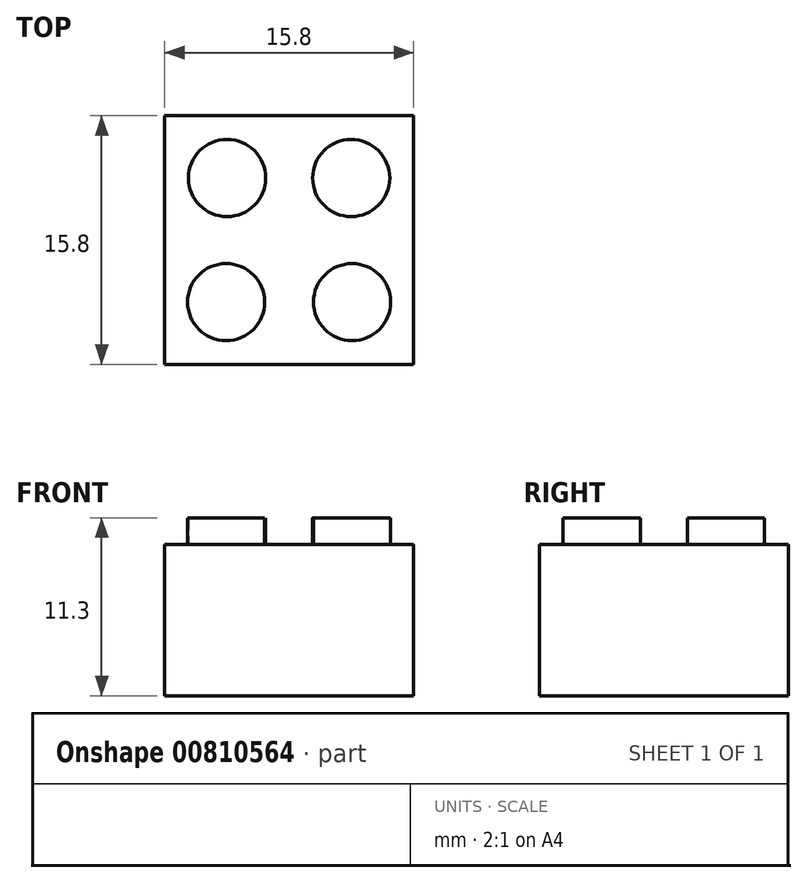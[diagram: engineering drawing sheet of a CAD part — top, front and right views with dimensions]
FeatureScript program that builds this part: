
annotation { "Feature Type Name" : "Feature", "Feature Type Description" : "" }
export const myFeature = defineFeature(function(context is Context, id is Id, definition is map)
    precondition{}
    {
        {
            var Q0;
            Q0=qCreatedBy(makeId("Top.planeOp"),FACE);
            var sketch = newSketch(context, id + "F0", { "sketchPlane" : qUnion([Q0])});
            skLineSegment(sketch, "E0", {"start": v(0, 0) * mm, "end": v(0, 15.8) * mm});
            skLineSegment(sketch, "E1", {"start": v(0, 15.8) * mm, "end": v(15.8, 15.8) * mm});
            skLineSegment(sketch, "E2", {"start": v(15.8, 15.8) * mm, "end": v(15.8, 0) * mm});
            skLineSegment(sketch, "E3", {"start": v(15.8, 0) * mm, "end": v(0, 0) * mm});
            skSolve(sketch);
        }
        {
            var Q0;
            Q0=makeQuery(id+"F0.imprint","IMPRINT",FACE,{"disambiguationData":[TD([[makeQuery(id+"F0.imprint","IMPRINT",EDGE,{"derivedFrom":sQuery(id+"F0.wireOp",EDGE,"E0")}),-1.0]])]});
            extrude(context, id + "F1", {"entities" : qUnion([Q0]), "depth" : 9.6 * mm, "offsetDistance" : 25.4 * mm});
        }
        {
            var Q0;
            Q0=makeQuery(id+"F1.opExtrude","CAP_FACE",FACE,{"disambiguationData":[OSD([sQuery(id+"F0.wireOp",EDGE,"E0"),sQuery(id+"F0.wireOp",EDGE,"E1"),sQuery(id+"F0.wireOp",EDGE,"E2"),sQuery(id+"F0.wireOp",EDGE,"E3")])],"isStart":false});
            var sketch = newSketch(context, id + "F2", { "sketchPlane" : qUnion([Q0])});
            skLineSegment(sketch, "E4", {"start": v(0, 0) * mm, "end": v(3.9, 0) * mm, "construction": true});
            skLineSegment(sketch, "E5", {"start": v(15.8, 0) * mm, "end": v(11.9, 0) * mm, "construction": true});
            skLineSegment(sketch, "E6", {"start": v(3.9, 0) * mm, "end": v(3.9, 3.96) * mm, "construction": true});
            skLineSegment(sketch, "E7", {"start": v(11.9, 0) * mm, "end": v(11.9, 3.96) * mm, "construction": true});
            skCircle(sketch, "E8", {"center": v(11.9, 3.96) * mm, "radius": 2.45 * mm});
            skCircle(sketch, "E9", {"center": v(3.9, 3.96) * mm, "radius": 2.45 * mm});
            skLineSegment(sketch, "E10", {"start": v(15.8, 15.8) * mm, "end": v(11.84, 15.8) * mm, "construction": true});
            skLineSegment(sketch, "E11", {"start": v(0, 15.8) * mm, "end": v(3.96, 15.8) * mm, "construction": true});
            skLineSegment(sketch, "E12", {"start": v(3.96, 15.8) * mm, "end": v(3.96, 11.84) * mm, "construction": true});
            skLineSegment(sketch, "E13", {"start": v(11.84, 15.8) * mm, "end": v(11.84, 11.84) * mm, "construction": true});
            skCircle(sketch, "E14", {"center": v(3.96, 11.84) * mm, "radius": 2.45 * mm});
            skCircle(sketch, "E15", {"center": v(11.84, 11.84) * mm, "radius": 2.45 * mm});
            skSolve(sketch);
        }
        {
            var Q0;
            Q0=makeQuery(id+"F2.imprint","IMPRINT",FACE,{"disambiguationData":[TD([[makeQuery(id+"F2.imprint","IMPRINT",EDGE,{"derivedFrom":sQuery(id+"F2.wireOp",EDGE,"E14")}),1.0]])]});
            var Q1;
            Q1=makeQuery(id+"F2.imprint","IMPRINT",FACE,{"disambiguationData":[TD([[makeQuery(id+"F2.imprint","IMPRINT",EDGE,{"derivedFrom":sQuery(id+"F2.wireOp",EDGE,"E15")}),1.0]])]});
            var Q2;
            Q2=makeQuery(id+"F2.imprint","IMPRINT",FACE,{"disambiguationData":[TD([[makeQuery(id+"F2.imprint","IMPRINT",EDGE,{"derivedFrom":sQuery(id+"F2.wireOp",EDGE,"E8")}),1.0]])]});
            var Q3;
            Q3=makeQuery(id+"F2.imprint","IMPRINT",FACE,{"disambiguationData":[TD([[makeQuery(id+"F2.imprint","IMPRINT",EDGE,{"derivedFrom":sQuery(id+"F2.wireOp",EDGE,"E9")}),1.0]])]});
            extrude(context, id + "F3", {"entities" : qUnion([Q0, Q1, Q2, Q3]), "operationType" : NewBodyOperationType.ADD, "depth" : 1.7 * mm, "offsetDistance" : 25.4 * mm});
        }
    });
